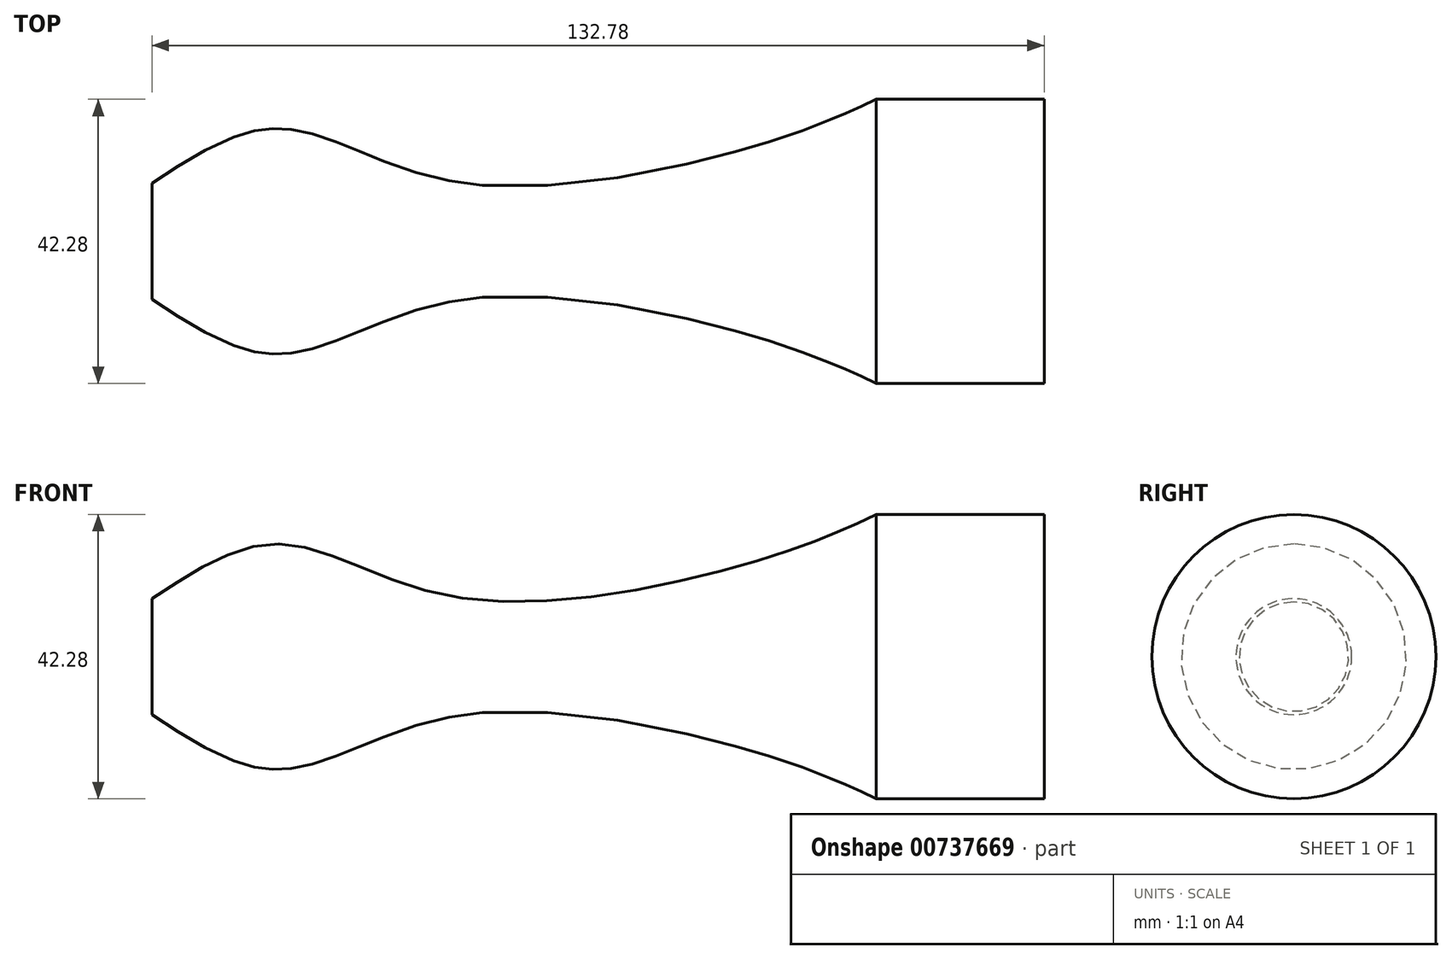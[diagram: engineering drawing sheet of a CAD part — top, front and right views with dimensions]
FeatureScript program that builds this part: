
annotation { "Feature Type Name" : "Feature", "Feature Type Description" : "" }
export const myFeature = defineFeature(function(context is Context, id is Id, definition is map)
    precondition{}
    {
        {
            var Q0;
            Q0=qCreatedBy(makeId("Top.planeOp"),FACE);
            var sketch = newSketch(context, id + "F0", { "sketchPlane" : qUnion([Q0])});
            skFitSpline(sketch, "E0", {"points": [v(-64.69, 8.62) * mm, v(-45.64, 16.78) * mm, v(-19.32, 8.8) * mm, v(27.67, 14.97) * mm, v(43.1, 21.14) * mm], "startDerivative": vector(85.95, 57.03) * mm, "endDerivative": vector(63.55, 29.8) * mm});
            skLineSegment(sketch, "E1", {"start": v(-64.69, 8.62) * mm, "end": v(-64.69, 0) * mm});
            skLineSegment(sketch, "E2", {"start": v(-64.69, 0) * mm, "end": v(43.1, 0) * mm});
            skLineSegment(sketch, "E3", {"start": v(43.1, 0) * mm, "end": v(43.1, 21.14) * mm});
            skSolve(sketch);
        }
        {
            var Q0;
            Q0=makeQuery(id+"F0.imprint","IMPRINT",FACE,{"disambiguationData":[TD([[makeQuery(id+"F0.imprint","IMPRINT",EDGE,{"derivedFrom":sQuery(id+"F0.wireOp",EDGE,"E0")}),-1.0]])]});
            var Q1;
            Q1=sQuery(id+"F0.wireOp",EDGE,"E2");
            revolve(context, id + "F1", {"surfaceOperationType" : NewSurfaceOperationType.NEW, "entities" : qUnion([Q0]), "axis" : qUnion([Q1]), "revolveType" : RevolveType.FULL});
        }
        {
            var Q0;
            Q0=makeQuery(id+"F1.opRevolve","SWEPT_FACE",FACE,{"disambiguationData":[OSD([sQuery(id+"F0.wireOp",EDGE,"E3")])]});
            extrude(context, id + "F2", {"entities" : qUnion([Q0]), "operationType" : NewBodyOperationType.ADD, "depth" : 25 * mm, "offsetDistance" : 25 * mm});
        }
    });
